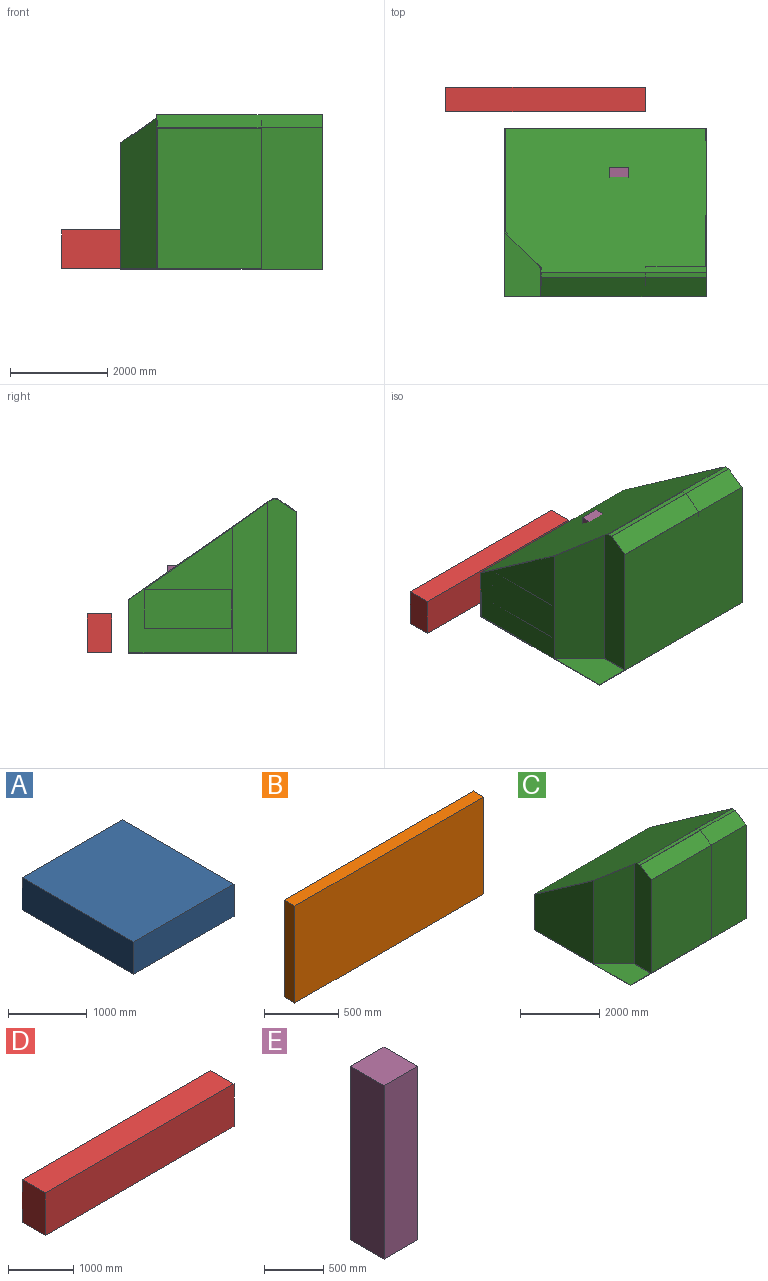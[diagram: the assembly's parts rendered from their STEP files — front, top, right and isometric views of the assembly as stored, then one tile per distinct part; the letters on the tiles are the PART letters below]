
ASSEMBLY  parts=5 mates=4
PART A: 6 faces, bbox 1800x2000x500 mm
  f0: plane 1800x500mm, normal (0,-1,0), area 900000mm2, adj f1,f3,f4,f5
  f1: plane 2000x500mm, normal (1,0,0), area 1000000mm2, adj f0,f2,f4,f5
  f2: plane 1800x500mm, normal (0,1,0), area 900000mm2, adj f1,f3,f4,f5
  f3: plane 2000x500mm, normal (-1,0,0), area 1000000mm2, adj f0,f2,f4,f5
  f4: plane 2000x1800mm, normal (0,0,1), area 3600000mm2, adj f0,f1,f2,f3
  f5: plane 2000x1800mm, normal (0,0,-1), area 3600000mm2, adj f0,f1,f2,f3
PART B: 6 faces, bbox 1800x100x800 mm
  f0: plane 1800x100mm, normal (0,0,-1), area 180000mm2, adj f1,f3,f4,f5
  f1: plane 800x100mm, normal (1,0,0), area 80000mm2, adj f0,f2,f4,f5
  f2: plane 1800x100mm, normal (0,0,1), area 180000mm2, adj f1,f3,f4,f5
  f3: plane 800x100mm, normal (-1,0,0), area 80000mm2, adj f0,f2,f4,f5
  f4: plane 1800x800mm, normal (0,-1,0), area 1440000mm2, adj f0,f1,f2,f3
  f5: plane 1800x800mm, normal (0,1,0), area 1440000mm2, adj f0,f1,f2,f3
PART C: 32 faces, bbox 4138.8x3450x3175.6 mm
  f0: plane 4138.77x2904.74mm, normal (0,-1,0), area 9883394.6mm2, adj f2,f3,f4,f6,f8,f10
  f1: plane 3399.96x106.31mm, normal (0,0,1), area 361436.4mm2, adj f2,f4,f5,f8
  f2: plane 3399.96x386.85mm, normal (0,-0.57,0.82), area 1605642.9mm2, adj f0,f1,f4,f8
  f3: plane 3450x2598.19mm, normal (-1,0,0), area 3961383.6mm2, adj f0,f5,f6,f7,f9,f10
  f4: plane 3450x3175.61mm, normal (1,0,0), area 7842531.2mm2, adj f0,f1,f2,f5,f6,f7
  f5: plane 4138.77x2956.85mm, normal (0,0.57,0.82), area 14525803.8mm2, adj f1,f3,f4,f7,f8,f9
  f6: plane 4138.77x3450mm, normal (0,0,-1), area 14278746mm2, adj f0,f3,f4,f7
  f7: plane 4138.77x1105.21mm, normal (0,1,0), area 4574188.7mm2, adj f3,f4,f5,f6
  f8: plane 3165.61x585.83mm, normal (-1,0,0), area 1799112.2mm2, adj f0,f1,f2,f5,f9,f10
  f9: plane 3100.72x738.8mm, normal (-0.7,-0.71,0), area 2958234mm2, adj f3,f5,f8,f10
  f10: plane 1317.79x738.8mm, normal (0,0,1), area 703202mm2, adj f0,f3,f8,f9
  f11: plane 3074.58x2834.28mm, normal (-1,0,0), area 3942046mm2, adj f16,f17,f18,f19,f26,f27,f28
  f12: plane 2889.53x2149.98mm, normal (0,1,0), area 6212429.6mm2, adj f15,f17,f20,f22
  f13: plane 2573.07x2118.04mm, normal (1,0,0), area 3879254.9mm2, adj f16,f17,f18,f21
  f14: plane 2149.98x100mm, normal (0,0,-1), area 214997.7mm2, adj f15,f16,f20,f22
  f15: plane 2149.98x380mm, normal (0,0.57,-0.82), area 997362.1mm2, adj f12,f14,f20,f22
  f16: plane 4118.77x2950mm, normal (0,-0.57,-0.82), area 14238820.2mm2, adj f11,f13,f14,f18,f19,f20,f21,f22
  f17: plane 4118.77x3430mm, normal (0,0,1), area 12685997.5mm2, adj f11,f12,f13,f18,f19,f20,f21,f22
  f18: plane 4118.77x1090mm, normal (0,-1,0), area 4489456mm2, adj f11,f13,f16,f17
  f19: plane 3074.58x1229.99mm, normal (0,1,0), area 3781696.9mm2, adj f11,f16,f17,f20
  f20: plane 3155.61x595.72mm, normal (-1,0,0), area 1824620.9mm2, adj f12,f14,f15,f16,f17,f19
  f21: plane 3085.59x738.8mm, normal (0.7,0.71,0), area 2942501.7mm2, adj f13,f16,f17,f22
  f22: plane 3155.61x580mm, normal (1,0,0), area 1776199.1mm2, adj f12,f14,f15,f16,f17,f21
  f23: plane 1810x10mm, normal (0,-1,0), area 18100mm2, adj f24,f29,f30,f31
  f24: plane 775x10mm, normal (0,0,-1), area 7750mm2, adj f23,f25,f30,f31
  f25: plane 1810x10mm, normal (0,1,0), area 18100mm2, adj f24,f29,f30,f31
  f26: plane 2010x10mm, normal (0,1,0), area 20100mm2, adj f11,f17,f28,f30
  f27: plane 2010x10mm, normal (0,-1,0), area 20100mm2, adj f11,f17,f28,f30
  f28: plane 975x10mm, normal (0,0,1), area 9750mm2, adj f11,f26,f27,f30
  f29: plane 775x10mm, normal (0,0,1), area 7750mm2, adj f23,f25,f30,f31
  f30: plane 2010x975mm, normal (-1,0,0), area 557000mm2, adj f17,f23,f24,f25,f26,f27,f28,f29
  f31: plane 1810x775mm, normal (-1,0,0), area 1402750mm2, adj f23,f24,f25,f29
PART D: 6 faces, bbox 4100x500x800 mm
  f0: plane 4100x800mm, normal (0,-1,0), area 3280000mm2, adj f1,f3,f4,f5
  f1: plane 800x500mm, normal (1,0,0), area 400000mm2, adj f0,f2,f4,f5
  f2: plane 4100x800mm, normal (0,1,0), area 3280000mm2, adj f1,f3,f4,f5
  f3: plane 800x500mm, normal (-1,0,0), area 400000mm2, adj f0,f2,f4,f5
  f4: plane 4100x500mm, normal (0,0,1), area 2050000mm2, adj f0,f1,f2,f3
  f5: plane 4100x500mm, normal (0,0,-1), area 2050000mm2, adj f0,f1,f2,f3
PART E: 6 faces, bbox 400x400x1800 mm
  f0: plane 1800x400mm, normal (0,-1,0), area 720000mm2, adj f1,f3,f4,f5
  f1: plane 1800x400mm, normal (1,0,0), area 720000mm2, adj f0,f2,f4,f5
  f2: plane 1800x400mm, normal (0,1,0), area 720000mm2, adj f1,f3,f4,f5
  f3: plane 1800x400mm, normal (-1,0,0), area 720000mm2, adj f0,f2,f4,f5
  f4: plane 400x400mm, normal (0,0,1), area 160000mm2, adj f0,f1,f2,f3
  f5: plane 400x400mm, normal (0,0,-1), area 160000mm2, adj f0,f1,f2,f3
PLACE A rot(axis=(0,0,-1),90deg) t=(-2505.55,-82.99,1110.01)mm
PLACE B rot(axis=(0,0,1),90deg) t=(-4307.2,998.38,2010.51)mm
PLACE C t=(-188.43,-625.18,1110.01)mm fixed
PLACE D t=(-3476.11,2811.21,1110.01)mm
PLACE E t=(-1967.89,1219.58,1110.01)mm
MATE planar B.f5 <-> C.f13  axis (-1,0,0) through (-4307.2,998.38,2010.51)mm
MATE planar A.f5 <-> C.f17  axis (0,0,-1) through (-2505.55,-82.99,1110.01)mm
MATE planar E.f5 <-> C.f17  axis (0,0,-1) through (-1967.89,1219.58,1110.01)mm
MATE planar D.f5 <-> C.f17  axis (0,0,-1) through (-3476.11,3061.21,1110.01)mm
